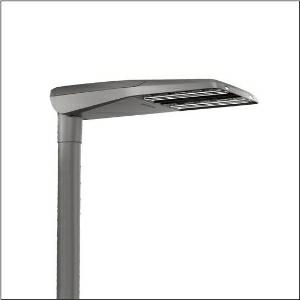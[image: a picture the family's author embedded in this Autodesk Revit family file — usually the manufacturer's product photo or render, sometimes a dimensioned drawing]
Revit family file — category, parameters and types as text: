
# Revit family: streetlight_sl_11_iq_midi___st1_2a_5xc3a41e08le_4284
name_source: partatom
category: Lighting Fixtures
units: mm (PartAtom-declared; Revit-internal decimal feet)

## family parameters
Cut with Voids When Loaded = No
Host = Face
Light Source = No
Part Type = Normal
Room Calculation Point = No
Round Connector Dimension = Use Diameter
Shared = No

## types (1)
- --- (1 x LED, 9590 lm, 60.4 W, 4000K)
    Apparent Load = 60 VA
    CIE Flux Codes = 32 70 96 100 100
    Color Rendering = 70
    Color Temperature = 4000K
    Default Elevation = 1800 mm
    Description = Streetlight SL 11 iQ midi, mast luminaire, primary light control with 3 zone facetted reflector, of plastic, silver coated, highly specular, primary optical cover: cover, of PMMA, transparent, light distribution: ST1.2a, light emission: direct distribution, primary light characteristic: asymmetric, installation type: post-top, side-entry, lamps: LED, High Power LED, rated values: 9.590lm | 60,4W | 158,8lm/W (begin service life); end service life: 9.590lm | 62,5W; at 50% lumin. flux: 4.795lm | 29,7W | 161,4lm/W, colour temperature: 4000K, colour rendering: CRI > 70, light colour: 740, light setting 1 begin service life: 100% | 9.590lm | 60,4W | 158,8lm/W | 4.000K, light setting 1 end service life: 62,5W, further light settings possible, control: optimised constant luminous flux control (CLO 2.0), Desk-Remote (wireless, voltage-free reading and setting of iQ features in the workshop via application-optimized NFC function/RFID function), Light-Fading, Smart-Wire, Night-Set, Lumen-Switch, Temp-Guard, Auto-Match, with cable H07RN-F 5x 1.5mm², mains connection: 230..240V, AC, 50/60Hz, connection cable pre-assembled, cable length: 8,5m, luminaire housing, of diecast aluminium, powder-coated, Siteco® metallic grey (DB 702S), please order mast flange separately, inclination adjustable without tools: 0°, 5°, 10°, 15° (post-top) | 0°, -5°, -10°, -15° (side-entry), sealing non-destructively replaceable, multi-level sealing system, length: 780mm, width: 376mm, height: 118mm, mast flange for spigot size: 42mm (side-entry): 5XC10008XM4, 60/48mm (side-entry/post-top): 5XC10108XM2, 76/60mm (side-entry/post-top): 5XC10108XM1, equipment: standard, protection rating (complete): IP66, insulation class (complete): insulation class II (safety insulation), certification: CE, ENEC, ENEC+, VDE, impact resistance: IK10, permissible operating ambient temperature for outdoor applications: -25..+50°C, standard-compliant lighting for roads and squares, Environmental Product Declaration (EPD) tested and certified by an independent institute, packaging unit: 1 piece

Light Distribution: ST1.2a
    Height = 118 mm
    Lamp = 1 x LED
    Lamp Light Flux = 9590 lm
    Lamp Power = 60.4 W
    Lamp count = 1
    Length = 780 mm
    Luminous efficacy = 159 lm/W
    Manufacturer = Siteco
    ModVariant = No
    Model = 5XC3A41E08LE
    Number of Poles = 1
    OnlyDefault = Yes
    Power Factor = 1
    Product Name = Streetlight SL 11 iQ midi | ST1.2a
    Product group = mast luminaire | pylon top
    ProductGroupID = 6100
    Protection Class = Protection class II
    Protection Degree = IP 66
    RLX_Detail_Level = 1
    RLX_Emergency_Light_Flux = 0 lm
    RLX_Emergency_Type = 0
    RLX_Emergency_Type_DB = No
    RlxData = <blob elided: 70737 chars, md5=5f936253>
    Socket = socket
    Standby Power = 0 W
    System Light Flux = 9590 lm
    System Power = 60 W
    Type Comments = factory setting: luminous flux: 100 % | dim-lin: 254 | 520 mA
    Type Image = l_1005960.jpg
    URL = http://relux.com
    VarID = @adj_197054
    Voltage = 0 V
    Weight = 0.00 kg
    Width = 376 mm

## geometry (parser evidence)
native form markers: Blend x4, Sweep x11
no freeform markers — native parametric forms only
